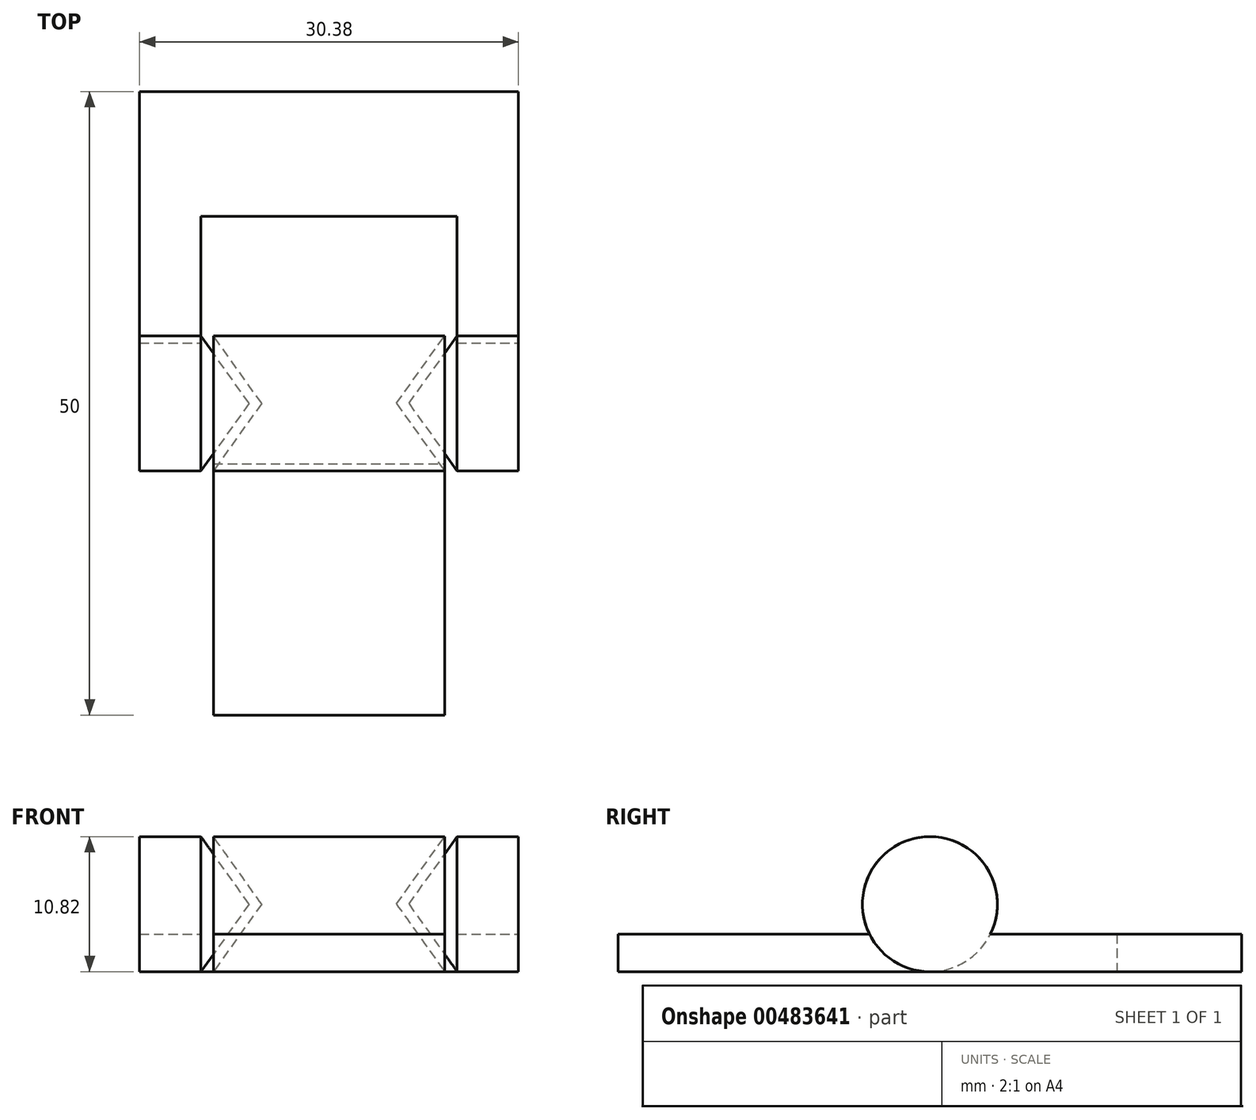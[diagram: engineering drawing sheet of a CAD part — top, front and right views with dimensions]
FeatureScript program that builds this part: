
annotation { "Feature Type Name" : "Feature", "Feature Type Description" : "" }
export const myFeature = defineFeature(function(context is Context, id is Id, definition is map)
    precondition{}
    {
        {
            var Q0;
            Q0=qCreatedBy(makeId("Top.planeOp"),FACE);
            var sketch = newSketch(context, id + "F0", { "sketchPlane" : qUnion([Q0])});
            skLineSegment(sketch, "E0", {"start": v(0, 0) * mm, "end": v(-5.4, 0) * mm});
            skLineSegment(sketch, "E1", {"start": v(-5.4, 0) * mm, "end": v(-9.28, 5.41) * mm});
            skLineSegment(sketch, "E2", {"start": v(-9.28, 5.41) * mm, "end": v(0, 5.41) * mm});
            skLineSegment(sketch, "E3", {"start": v(0, 5.41) * mm, "end": v(0, 0) * mm});
            skLineSegment(sketch, "E4", {"start": v(-6.4, 0) * mm, "end": v(-10.28, 5.41) * mm});
            skLineSegment(sketch, "E5", {"start": v(-10.28, 5.41) * mm, "end": v(-15.19, 5.41) * mm});
            skLineSegment(sketch, "E6", {"start": v(-15.19, 5.41) * mm, "end": v(-15.19, 0) * mm});
            skLineSegment(sketch, "E7", {"start": v(-15.19, 0) * mm, "end": v(-6.4, 0) * mm});
            skLineSegment(sketch, "E8.MirrorCS", {"start": v(10.28, 5.41) * mm, "end": v(15.19, 5.41) * mm});
            skLineSegment(sketch, "E9.MirrorCS", {"start": v(6.4, 0) * mm, "end": v(10.28, 5.41) * mm});
            skLineSegment(sketch, "E10.MirrorCS", {"start": v(15.19, 0) * mm, "end": v(6.4, 0) * mm});
            skLineSegment(sketch, "E11.MirrorCS", {"start": v(15.19, 5.41) * mm, "end": v(15.19, 0) * mm});
            skLineSegment(sketch, "E12.MirrorCS", {"start": v(5.4, 0) * mm, "end": v(9.28, 5.41) * mm});
            skLineSegment(sketch, "E13.MirrorCS", {"start": v(9.28, 5.41) * mm, "end": v(0, 5.41) * mm});
            skLineSegment(sketch, "E14.MirrorCS", {"start": v(0, 0) * mm, "end": v(5.4, 0) * mm});
            skSolve(sketch);
        }
        {
            var Q0;
            Q0=makeQuery(id+"F0.imprint","IMPRINT",FACE,{"disambiguationData":[TD([[makeQuery(id+"F0.imprint","IMPRINT",EDGE,{"derivedFrom":sQuery(id+"F0.wireOp",EDGE,"E4")}),1.0]])]});
            var Q1;
            Q1=makeQuery(id+"F0.imprint","IMPRINT",FACE,{"disambiguationData":[TD([[makeQuery(id+"F0.imprint","IMPRINT",EDGE,{"derivedFrom":sQuery(id+"F0.wireOp",EDGE,"E0")}),-1.0]])]});
            var Q2;
            Q2=makeQuery(id+"F0.imprint","IMPRINT",FACE,{"disambiguationData":[TD([[makeQuery(id+"F0.imprint","IMPRINT",EDGE,{"derivedFrom":sQuery(id+"F0.wireOp",EDGE,"E3")}),1.0]])]});
            var Q3;
            Q3=makeQuery(id+"F0.imprint","IMPRINT",FACE,{"disambiguationData":[TD([[makeQuery(id+"F0.imprint","IMPRINT",EDGE,{"derivedFrom":sQuery(id+"F0.wireOp",EDGE,"E8.MirrorCS")}),-1.0]])]});
            var Q4;
            Q4=sQuery(id+"F0.wireOp",EDGE,"E0");
            revolve(context, id + "F1", {"entities" : qUnion([Q0, Q1, Q2, Q3]), "axis" : qUnion([Q4]), "revolveType" : RevolveType.FULL});
        }
        {
            var Q0;
            Q0=qCreatedBy(makeId("Front.planeOp"),FACE);
            cPlane(context, id + "F2", {"entities" : qUnion([Q0]), "cplaneType" : CPlaneType.OFFSET, "offset" : 25 * mm, "width" : 150 * mm, "height" : 150 * mm});
        }
        {
            var Q0;
            Q0=qCreatedBy(makeId("Front.planeOp"),FACE);
            cPlane(context, id + "F3", {"entities" : qUnion([Q0]), "cplaneType" : CPlaneType.OFFSET, "offset" : 25 * mm, "oppositeDirection" : true, "width" : 150 * mm, "height" : 150 * mm});
        }
        {
            var Q0;
            Q0=qCreatedBy(id+"F2.planeOp",FACE);
            var sketch = newSketch(context, id + "F4", { "sketchPlane" : qUnion([Q0])});
            skLineSegment(sketch, "E15", {"start": v(9.28, -5.41) * mm, "end": v(-9.28, -5.41) * mm});
            skLineSegment(sketch, "E16.bottom", {"start": v(-9.28, -5.41) * mm, "end": v(9.28, -5.41) * mm});
            skLineSegment(sketch, "E16.top", {"start": v(-9.28, -2.41) * mm, "end": v(9.28, -2.41) * mm});
            skLineSegment(sketch, "E16.left", {"start": v(-9.28, -5.41) * mm, "end": v(-9.28, -2.41) * mm});
            skLineSegment(sketch, "E16.right", {"start": v(9.28, -5.41) * mm, "end": v(9.28, -2.41) * mm});
            skSolve(sketch);
        }
        {
            var Q0;
            Q0 = qSketchRegion(id + "F4", true);
            var Q1;
            Q1=makeQuery(id+"F1.opRevolve","SWEPT_FACE",FACE,{"disambiguationData":[OSD([sQuery(id+"F0.wireOp",EDGE,"E2"),sQuery(id+"F0.wireOp",EDGE,"E13.MirrorCS")])]});
            extrude(context, id + "F5", {"entities" : qUnion([Q0]), "operationType" : NewBodyOperationType.ADD, "endBound" : BoundingType.UP_TO_SURFACE, "oppositeDirection" : true, "endBoundEntityFace" : qUnion([Q1]), "depth" : 25 * mm});
        }
        {
            var Q0;
            Q0=qCreatedBy(id+"F3.planeOp",FACE);
            var sketch = newSketch(context, id + "F6", { "sketchPlane" : qUnion([Q0])});
            skLineSegment(sketch, "E17.0", {"start": v(15.19, 5.41) * mm, "end": v(15.19, -5.41) * mm});
            skLineSegment(sketch, "E18.0", {"start": v(10.28, 5.41) * mm, "end": v(10.28, -5.41) * mm});
            skLineSegment(sketch, "E19", {"start": v(15.19, -5.41) * mm, "end": v(10.28, -5.41) * mm});
            skLineSegment(sketch, "E20.0", {"start": v(-10.28, 5.41) * mm, "end": v(-10.28, -5.41) * mm});
            skLineSegment(sketch, "E21", {"start": v(-10.28, -5.41) * mm, "end": v(-15.19, -5.41) * mm});
            skLineSegment(sketch, "E22.0", {"start": v(-15.19, 5.41) * mm, "end": v(-15.19, -5.41) * mm});
            skLineSegment(sketch, "E23", {"start": v(15.19, -2.41) * mm, "end": v(-15.19, -2.41) * mm});
            skSolve(sketch);
        }
        {
            var Q0;
            {var subQ0=sQuery(id+"F6.wireOp",EDGE,"E19");Q0=makeQuery(id+"F6.imprint","IMPRINT",FACE,{"disambiguationData":[TD([[makeQuery(id+"F6.imprint","IMPRINT",EDGE,{"derivedFrom":subQ0}),-1.0]])]});}
            var Q1;
            {var subQ0=sQuery(id+"F6.wireOp",EDGE,"E21");Q1=makeQuery(id+"F6.imprint","IMPRINT",FACE,{"disambiguationData":[TD([[makeQuery(id+"F6.imprint","IMPRINT",EDGE,{"derivedFrom":subQ0}),-1.0]])]});}
            extrude(context, id + "F7", {"entities" : qUnion([Q0, Q1]), "operationType" : NewBodyOperationType.ADD, "endBound" : BoundingType.UP_TO_NEXT, "depth" : 25 * mm});
        }
        {
            var Q0;
            {var subQ0=sQuery(id+"F6.wireOp",EDGE,"E23");Q0=makeQuery(id+"F7.opExtrude","SWEPT_FACE",FACE,{"disambiguationData":[OSD([subQ0]),TDD([makeQuery(id+"F6.imprint","IMPRINT",EDGE,{"disambiguationData":[TD([[makeQuery(id+"F6.imprint","INTERSECT",VERTEX,{"derivedFrom":[sQuery(id+"F6.wireOp",EDGE,"E22.0"),subQ0]}),1.0]])],"derivedFrom":subQ0})])]});}
            var sketch = newSketch(context, id + "F8", { "sketchPlane" : qUnion([Q0])});
            skLineSegment(sketch, "E24.0", {"start": v(-15.19, 4.85) * mm, "end": v(-15.19, 25) * mm});
            skLineSegment(sketch, "E24.1", {"start": v(15.19, 4.85) * mm, "end": v(15.19, 25) * mm});
            skLineSegment(sketch, "E24.2", {"start": v(15.19, 25) * mm, "end": v(10.28, 25) * mm});
            skLineSegment(sketch, "E24.3", {"start": v(-10.28, 25) * mm, "end": v(-15.19, 25) * mm});
            skLineSegment(sketch, "E25", {"start": v(-10.28, 25) * mm, "end": v(10.28, 25) * mm});
            skLineSegment(sketch, "E26", {"start": v(-15.19, 15) * mm, "end": v(15.19, 15) * mm});
            skSolve(sketch);
        }
        {
            var Q0;
            Q0 = qSketchRegion(id + "F8", true);
            var Q1;
            Q1=makeQuery(id+"F7.opExtrude","SWEPT_FACE",FACE,{"disambiguationData":[OSD([sQuery(id+"F6.wireOp",EDGE,"E21")])]});
            extrude(context, id + "F9", {"entities" : qUnion([Q0]), "operationType" : NewBodyOperationType.ADD, "endBound" : BoundingType.UP_TO_SURFACE, "oppositeDirection" : true, "endBoundEntityFace" : qUnion([Q1]), "depth" : 25 * mm});
        }
    });
